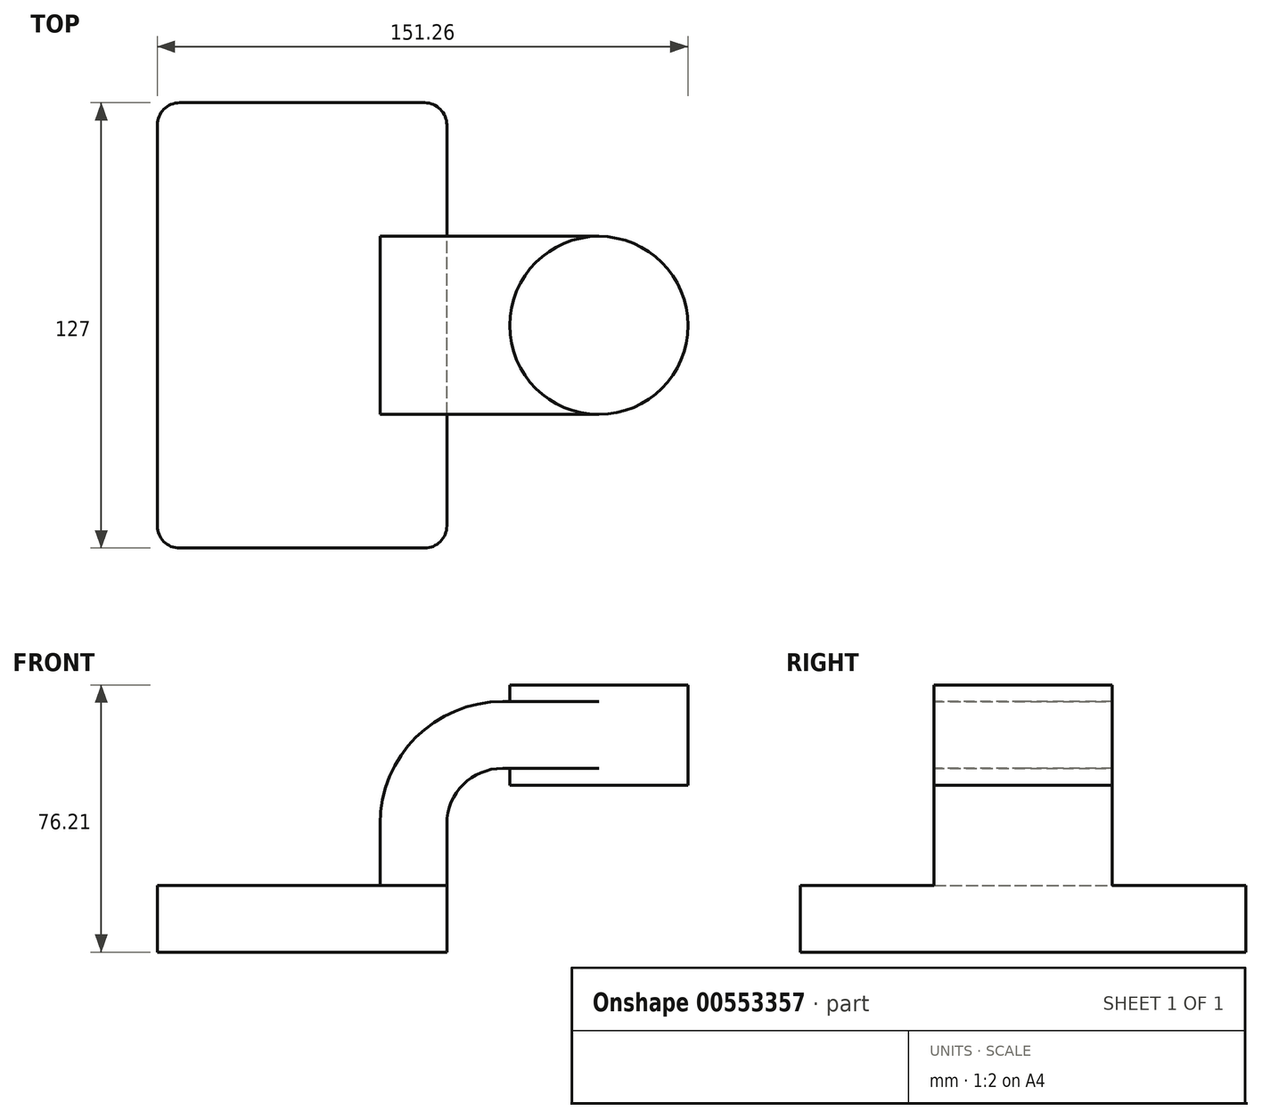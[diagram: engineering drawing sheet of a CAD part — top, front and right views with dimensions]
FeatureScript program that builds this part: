
annotation { "Feature Type Name" : "Feature", "Feature Type Description" : "" }
export const myFeature = defineFeature(function(context is Context, id is Id, definition is map)
    precondition{}
    {
        {
            var Q0;
            Q0=qCreatedBy(makeId("Front.planeOp"),FACE);
            var sketch = newSketch(context, id + "F0", { "sketchPlane" : qUnion([Q0])});
            skLineSegment(sketch, "E0.bottom", {"start": v(41.27, 9.53) * mm, "end": v(-41.28, 9.53) * mm});
            skLineSegment(sketch, "E0.top", {"start": v(41.28, -9.52) * mm, "end": v(-41.27, -9.52) * mm});
            skLineSegment(sketch, "E0.left", {"start": v(41.28, 9.53) * mm, "end": v(41.28, -9.52) * mm});
            skLineSegment(sketch, "E0.right", {"start": v(-41.28, 9.53) * mm, "end": v(-41.27, -9.52) * mm});
            skPoint(sketch, "E0.middle", {"position": v(0, 0) * mm});
            skLineSegment(sketch, "E1.bottom", {"start": v(109.99, 66.68) * mm, "end": v(59.19, 66.68) * mm});
            skLineSegment(sketch, "E1.top", {"start": v(109.99, 38.1) * mm, "end": v(59.19, 38.1) * mm});
            skLineSegment(sketch, "E1.left", {"start": v(109.99, 66.68) * mm, "end": v(109.99, 38.1) * mm});
            skLineSegment(sketch, "E1.right", {"start": v(59.19, 66.68) * mm, "end": v(59.19, 38.1) * mm});
            skPoint(sketch, "E1.middle", {"position": v(84.59, 52.39) * mm});
            skLineSegment(sketch, "E2", {"start": v(41.27, 9.53) * mm, "end": v(41.27, 27) * mm});
            skArc(sketch, "E3", {"start": v(41.27, 27) * mm, "mid": v(45.92, 38.23) * mm, "end": v(57.15, 42.88) * mm});
            skLineSegment(sketch, "E4", {"start": v(57.15, 42.88) * mm, "end": v(84.59, 42.88) * mm});
            skLineSegment(sketch, "E5.0", {"start": v(57.15, 61.93) * mm, "end": v(84.59, 61.93) * mm});
            skArc(sketch, "E5.1", {"start": v(22.23, 27) * mm, "mid": v(32.45, 51.7) * mm, "end": v(57.15, 61.93) * mm});
            skLineSegment(sketch, "E5.2", {"start": v(22.22, 9.53) * mm, "end": v(22.22, 27) * mm});
            skFitSpline(sketch, "E6", {"points": [v(-41.28, 9.53) * mm, v(57.15, 61.93) * mm], "startDerivative": vector(0, 104.6) * mm, "endDerivative": vector(81.82, 0) * mm});
            skLineSegment(sketch, "E7", {"start": v(84.59, 38.1) * mm, "end": v(84.59, 66.68) * mm});
            skSolve(sketch);
        }
        {
            var Q0;
            Q0=makeQuery(id+"F0.imprint","IMPRINT",FACE,{"disambiguationData":[TD([[makeQuery(id+"F0.imprint","IMPRINT",EDGE,{"derivedFrom":sQuery(id+"F0.wireOp",EDGE,"E0.top")}),-1.0]])]});
            extrude(context, id + "F1", {"entities" : qUnion([Q0]), "endBound" : BoundingType.SYMMETRIC, "depth" : 127 * mm, "offsetDistance" : 25.4 * mm});
        }
        {
            var Q0;
            {var subQ1=sQuery(id+"F0.wireOp",EDGE,"E2");Q0=makeQuery(id+"F0.imprint","IMPRINT",FACE,{"disambiguationData":[TD([[makeQuery(id+"F0.imprint","IMPRINT",EDGE,{"derivedFrom":subQ1}),1.0]])]});}
            var Q1;
            {var subQ0=sQuery(id+"F0.wireOp",EDGE,"E5.0");var subQ1=sQuery(id+"F0.wireOp",EDGE,"E1.right");var subQ2=makeQuery(id+"F0.imprint","INTERSECT",VERTEX,{"derivedFrom":[subQ1,subQ0]});Q1=makeQuery(id+"F0.imprint","IMPRINT",FACE,{"disambiguationData":[TD([[makeQuery(id+"F0.imprint","IMPRINT",EDGE,{"disambiguationData":[TD([[subQ2,-1.0]])],"derivedFrom":subQ1}),1.0]])]});}
            extrude(context, id + "F2", {"entities" : qUnion([Q0, Q1]), "operationType" : NewBodyOperationType.ADD, "endBound" : BoundingType.SYMMETRIC, "depth" : 50.8 * mm, "offsetDistance" : 25.4 * mm});
        }
        {
            var Q0;
            Q0=makeQuery(id+"F0.imprint","IMPRINT",FACE,{"disambiguationData":[TD([[makeQuery(id+"F0.imprint","IMPRINT",EDGE,{"derivedFrom":sQuery(id+"F0.wireOp",EDGE,"E5.1")}),1.0]])]});
            extrude(context, id + "F3", {"entities" : qUnion([Q0]), "operationType" : NewBodyOperationType.ADD, "endBound" : BoundingType.SYMMETRIC, "depth" : 15.88 * mm, "offsetDistance" : 25.4 * mm});
        }
        {
            var Q0;
            {var subQ0=sQuery(id+"F0.wireOp",EDGE,"E1.left");Q0=makeQuery(id+"F0.imprint","IMPRINT",FACE,{"disambiguationData":[TD([[makeQuery(id+"F0.imprint","IMPRINT",EDGE,{"derivedFrom":subQ0}),-1.0]])]});}
            var Q1;
            Q1=sQuery(id+"F0.wireOp",EDGE,"E7");
            revolve(context, id + "F4", {"operationType" : NewBodyOperationType.ADD, "entities" : qUnion([Q0]), "axis" : qUnion([Q1]), "revolveType" : RevolveType.FULL});
        }
        {
            var Q0;
            Q0=makeQuery(id+"F1.opExtrude","CAP_EDGE",EDGE,{"disambiguationData":[OSD([sQuery(id+"F0.wireOp",EDGE,"E0.left")])],"isStart":false});
            var Q1;
            Q1=makeQuery(id+"F1.opExtrude","CAP_EDGE",EDGE,{"disambiguationData":[OSD([sQuery(id+"F0.wireOp",EDGE,"E0.right")])],"isStart":false});
            var Q2;
            Q2=makeQuery(id+"F1.opExtrude","CAP_EDGE",EDGE,{"disambiguationData":[OSD([sQuery(id+"F0.wireOp",EDGE,"E0.left")])],"isStart":true});
            var Q3;
            Q3=makeQuery(id+"F1.opExtrude","CAP_EDGE",EDGE,{"disambiguationData":[OSD([sQuery(id+"F0.wireOp",EDGE,"E0.right")])],"isStart":true});
            fillet(context, id + "F5", {"entities" : qUnion([Q0, Q1, Q2, Q3]), "radius" : 6.35 * mm, "tangentPropagation" : true, "allowEdgeOverflow" : false});
        }
    });
